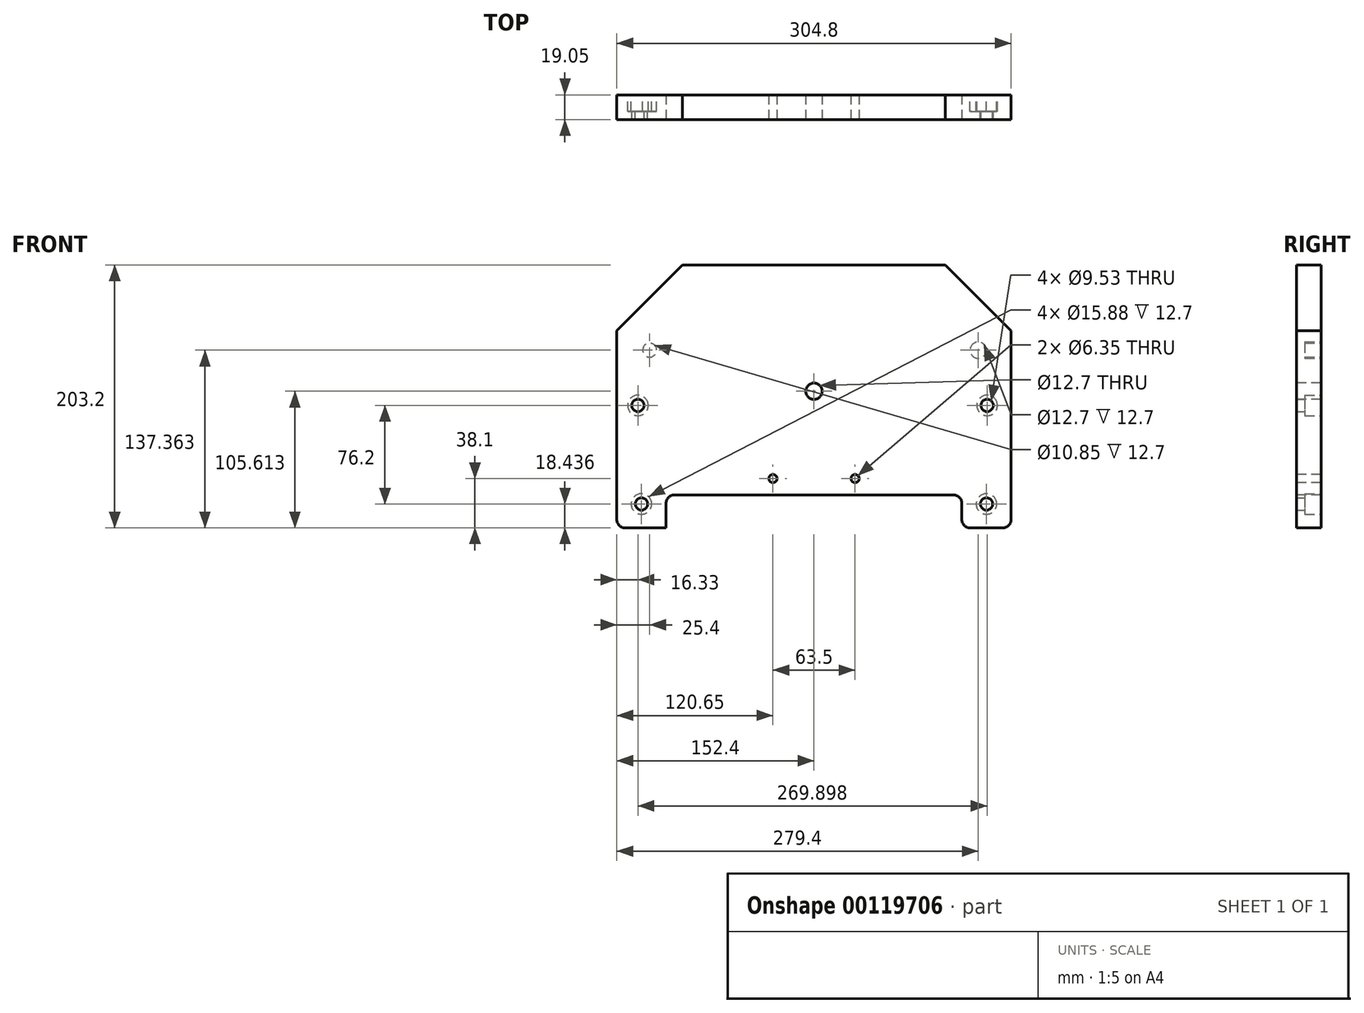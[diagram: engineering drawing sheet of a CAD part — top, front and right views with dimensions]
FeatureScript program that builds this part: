
annotation { "Feature Type Name" : "Feature", "Feature Type Description" : "" }
export const myFeature = defineFeature(function(context is Context, id is Id, definition is map)
    precondition{}
    {
        {
            var Q0;
            Q0=qCreatedBy(makeId("Front.planeOp"),FACE);
            var sketch = newSketch(context, id + "F0", { "sketchPlane" : qUnion([Q0])});
            skLineSegment(sketch, "E0.bottom", {"start": v(0, 0) * mm, "end": v(304.8, 0) * mm});
            skLineSegment(sketch, "E0.top", {"start": v(0, 203.2) * mm, "end": v(304.8, 203.2) * mm});
            skLineSegment(sketch, "E0.left", {"start": v(0, 0) * mm, "end": v(0, 203.2) * mm});
            skLineSegment(sketch, "E0.right", {"start": v(304.8, 0) * mm, "end": v(304.8, 203.2) * mm});
            skSolve(sketch);
        }
        {
            var Q0;
            Q0 = qSketchRegion(id + "F0", true);
            extrude(context, id + "F1", {"entities" : qUnion([Q0]), "depth" : 19.05 * mm});
        }
        {
            var Q0;
            Q0=makeQuery(id+"F1.opExtrude","CAP_FACE",FACE,{"disambiguationData":[OSD([sQuery(id+"F0.wireOp",EDGE,"E0.bottom"),sQuery(id+"F0.wireOp",EDGE,"E0.top"),sQuery(id+"F0.wireOp",EDGE,"E0.left"),sQuery(id+"F0.wireOp",EDGE,"E0.right")])],"isStart":false});
            var sketch = newSketch(context, id + "F2", { "sketchPlane" : qUnion([Q0])});
            skLineSegment(sketch, "E1.bottom", {"start": v(38.1, 0) * mm, "end": v(266.7, 0) * mm});
            skLineSegment(sketch, "E1.top", {"start": v(38.1, 25.4) * mm, "end": v(266.7, 25.4) * mm});
            skLineSegment(sketch, "E1.left", {"start": v(38.1, 0) * mm, "end": v(38.1, 25.4) * mm});
            skLineSegment(sketch, "E1.right", {"start": v(266.7, 0) * mm, "end": v(266.7, 25.4) * mm});
            skSolve(sketch);
        }
        {
            var Q0;
            Q0 = qSketchRegion(id + "F2", true);
            extrude(context, id + "F3", {"entities" : qUnion([Q0]), "operationType" : NewBodyOperationType.REMOVE, "endBound" : BoundingType.THROUGH_ALL, "oppositeDirection" : true, "depth" : 25.4 * mm});
        }
        {
            var Q0;
            Q0=makeQuery(id+"F1.opExtrude","CAP_FACE",FACE,{"disambiguationData":[OSD([sQuery(id+"F0.wireOp",EDGE,"E0.bottom"),sQuery(id+"F0.wireOp",EDGE,"E0.top"),sQuery(id+"F0.wireOp",EDGE,"E0.left"),sQuery(id+"F0.wireOp",EDGE,"E0.right")])],"isStart":false});
            var sketch = newSketch(context, id + "F4", { "sketchPlane" : qUnion([Q0])});
            skLineSegment(sketch, "E2", {"start": v(152.4, 25.4) * mm, "end": v(152.4, 203.2) * mm, "construction": true});
            skPoint(sketch, "E3", {"position": v(120.65, 38.1) * mm});
            skPoint(sketch, "E4", {"position": v(184.15, 38.1) * mm});
            skLineSegment(sketch, "E5", {"start": v(120.65, 38.1) * mm, "end": v(184.15, 38.1) * mm, "construction": true});
            skSolve(sketch);
        }
        {
            var Q0;
            Q0=sQuery(id+"F4.wireOp",VERTEX,"E3");
            var Q1;
            Q1=sQuery(id+"F4.wireOp",VERTEX,"E4");
            var Q2;
            Q2=makeQuery(id+"F1.opExtrude","SWEPT_BODY",BODY,{"disambiguationData":[OSD([sQuery(id+"F0.wireOp",EDGE,"E0.bottom"),sQuery(id+"F0.wireOp",EDGE,"E0.top"),sQuery(id+"F0.wireOp",EDGE,"E0.left"),sQuery(id+"F0.wireOp",EDGE,"E0.right")])]});
            hole(context, id + "F5", {"style" : HoleStyle.SIMPLE, "endStyle" : HoleEndStyle.THROUGH, "holeDiameter" : 6.35 * mm, "locations" : qUnion([Q0, Q1]), "scope" : qUnion([Q2]), "isTappedThrough" : true});
        }
        {
            var Q0;
            Q0=makeQuery(id+"F3.boolean.opBoolean","COPY",EDGE,{"derivedFrom":makeQuery(id+"F3.opExtrude","SWEPT_EDGE",EDGE,{"disambiguationData":[OSD([sQuery(id+"F0.wireOp",EDGE,"E0.bottom"),sQuery(id+"F2.wireOp",EDGE,"E1.bottom"),sQuery(id+"F2.wireOp",EDGE,"E1.left")])]})});
            var Q1;
            Q1=makeQuery(id+"F3.boolean.opBoolean","COPY",EDGE,{"derivedFrom":makeQuery(id+"F3.opExtrude","SWEPT_EDGE",EDGE,{"disambiguationData":[OSD([sQuery(id+"F2.wireOp",EDGE,"E1.top"),sQuery(id+"F2.wireOp",EDGE,"E1.left")])]})});
            var Q2;
            Q2=makeQuery(id+"F1.opExtrude","SWEPT_EDGE",EDGE,{"disambiguationData":[OSD([sQuery(id+"F0.wireOp",EDGE,"E0.bottom"),sQuery(id+"F0.wireOp",EDGE,"E0.left")])]});
            var Q3;
            Q3=makeQuery(id+"F3.boolean.opBoolean","COPY",EDGE,{"derivedFrom":makeQuery(id+"F3.opExtrude","SWEPT_EDGE",EDGE,{"disambiguationData":[OSD([sQuery(id+"F2.wireOp",EDGE,"E1.top"),sQuery(id+"F2.wireOp",EDGE,"E1.right")])]})});
            var Q4;
            Q4=makeQuery(id+"F3.boolean.opBoolean","COPY",EDGE,{"derivedFrom":makeQuery(id+"F3.opExtrude","SWEPT_EDGE",EDGE,{"disambiguationData":[OSD([sQuery(id+"F0.wireOp",EDGE,"E0.bottom"),sQuery(id+"F2.wireOp",EDGE,"E1.bottom"),sQuery(id+"F2.wireOp",EDGE,"E1.right")])]})});
            var Q5;
            Q5=makeQuery(id+"F1.opExtrude","SWEPT_EDGE",EDGE,{"disambiguationData":[OSD([sQuery(id+"F0.wireOp",EDGE,"E0.bottom"),sQuery(id+"F0.wireOp",EDGE,"E0.right")])]});
            fillet(context, id + "F6", {"entities" : qUnion([Q0, Q1, Q2, Q3, Q4, Q5]), "radius" : 6.35 * mm, "tangentPropagation" : true, "allowEdgeOverflow" : false});
        }
        {
            var Q0;
            Q0=makeQuery(id+"F1.opExtrude","CAP_FACE",FACE,{"disambiguationData":[OSD([sQuery(id+"F0.wireOp",EDGE,"E0.bottom"),sQuery(id+"F0.wireOp",EDGE,"E0.top"),sQuery(id+"F0.wireOp",EDGE,"E0.left"),sQuery(id+"F0.wireOp",EDGE,"E0.right")])],"isStart":false});
            var sketch = newSketch(context, id + "F7", { "sketchPlane" : qUnion([Q0])});
            skLineSegment(sketch, "E6", {"start": v(152.4, 25.4) * mm, "end": v(152.4, 105.61) * mm, "construction": true});
            skPoint(sketch, "E7", {"position": v(152.4, 105.61) * mm});
            skSolve(sketch);
        }
        {
            var Q0;
            Q0=sQuery(id+"F7.wireOp",VERTEX,"E7");
            var Q1;
            Q1=makeQuery(id+"F1.opExtrude","SWEPT_BODY",BODY,{"disambiguationData":[OSD([sQuery(id+"F0.wireOp",EDGE,"E0.bottom"),sQuery(id+"F0.wireOp",EDGE,"E0.top"),sQuery(id+"F0.wireOp",EDGE,"E0.left"),sQuery(id+"F0.wireOp",EDGE,"E0.right")])]});
            hole(context, id + "F8", {"style" : HoleStyle.SIMPLE, "endStyle" : HoleEndStyle.THROUGH, "holeDiameter" : 12.7 * mm, "locations" : qUnion([Q0]), "scope" : qUnion([Q1]), "isTappedThrough" : true});
        }
        {
            var Q0;
            Q0=makeQuery(id+"F1.opExtrude","CAP_FACE",FACE,{"disambiguationData":[OSD([sQuery(id+"F0.wireOp",EDGE,"E0.bottom"),sQuery(id+"F0.wireOp",EDGE,"E0.top"),sQuery(id+"F0.wireOp",EDGE,"E0.left"),sQuery(id+"F0.wireOp",EDGE,"E0.right")])],"isStart":true});
            var sketch = newSketch(context, id + "F9", { "sketchPlane" : qUnion([Q0])});
            skLineSegment(sketch, "E8", {"start": v(-152.4, 105.61) * mm, "end": v(-152.4, 137.36) * mm, "construction": true});
            skCircle(sketch, "E9", {"center": v(-25.4, 137.36) * mm, "radius": 5.43 * mm});
            skCircle(sketch, "E10", {"center": v(-279.4, 137.36) * mm, "radius": 6.35 * mm});
            skLineSegment(sketch, "E11", {"start": v(-152.4, 137.36) * mm, "end": v(-279.4, 137.36) * mm, "construction": true});
            skSolve(sketch);
        }
        {
            var Q0;
            Q0 = qSketchRegion(id + "F9", true);
            extrude(context, id + "F10", {"entities" : qUnion([Q0]), "operationType" : NewBodyOperationType.REMOVE, "oppositeDirection" : true, "depth" : 12.7 * mm});
        }
        {
            var Q0;
            Q0=makeQuery(id+"F1.opExtrude","CAP_FACE",FACE,{"disambiguationData":[OSD([sQuery(id+"F0.wireOp",EDGE,"E0.bottom"),sQuery(id+"F0.wireOp",EDGE,"E0.top"),sQuery(id+"F0.wireOp",EDGE,"E0.left"),sQuery(id+"F0.wireOp",EDGE,"E0.right")])],"isStart":true});
            var sketch = newSketch(context, id + "F11", { "sketchPlane" : qUnion([Q0])});
            skPoint(sketch, "E12", {"position": v(-286.23, 94.64) * mm});
            skPoint(sketch, "E13", {"position": v(-285.75, 18.44) * mm});
            skPoint(sketch, "E14", {"position": v(-16.33, 94.64) * mm});
            skPoint(sketch, "E15", {"position": v(-19.05, 18.44) * mm});
            skSolve(sketch);
        }
        {
            var Q0;
            Q0=sQuery(id+"F11.wireOp",VERTEX,"E12");
            var Q1;
            Q1=sQuery(id+"F11.wireOp",VERTEX,"E13");
            var Q2;
            Q2=sQuery(id+"F11.wireOp",VERTEX,"E15");
            var Q3;
            Q3=sQuery(id+"F11.wireOp",VERTEX,"E14");
            var Q4;
            Q4=makeQuery(id+"F1.opExtrude","SWEPT_BODY",BODY,{"disambiguationData":[OSD([sQuery(id+"F0.wireOp",EDGE,"E0.bottom"),sQuery(id+"F0.wireOp",EDGE,"E0.top"),sQuery(id+"F0.wireOp",EDGE,"E0.left"),sQuery(id+"F0.wireOp",EDGE,"E0.right")])]});
            hole(context, id + "F12", {"style" : HoleStyle.C_BORE, "endStyle" : HoleEndStyle.THROUGH, "holeDiameter" : 9.52 * mm, "cBoreDiameter" : 15.88 * mm, "cBoreDepth" : 12.7 * mm, "locations" : qUnion([Q0, Q1, Q2, Q3]), "scope" : qUnion([Q4]), "isTappedThrough" : true});
        }
        {
            var Q0;
            Q0=makeQuery(id+"F1.opExtrude","SWEPT_EDGE",EDGE,{"disambiguationData":[OSD([sQuery(id+"F0.wireOp",EDGE,"E0.top"),sQuery(id+"F0.wireOp",EDGE,"E0.right")])]});
            var Q1;
            Q1=makeQuery(id+"F1.opExtrude","SWEPT_EDGE",EDGE,{"disambiguationData":[OSD([sQuery(id+"F0.wireOp",EDGE,"E0.top"),sQuery(id+"F0.wireOp",EDGE,"E0.left")])]});
            chamfer(context, id + "F13", {"entities" : qUnion([Q0, Q1]), "width" : 50.8 * mm, "tangentPropagation" : true});
        }
    });
